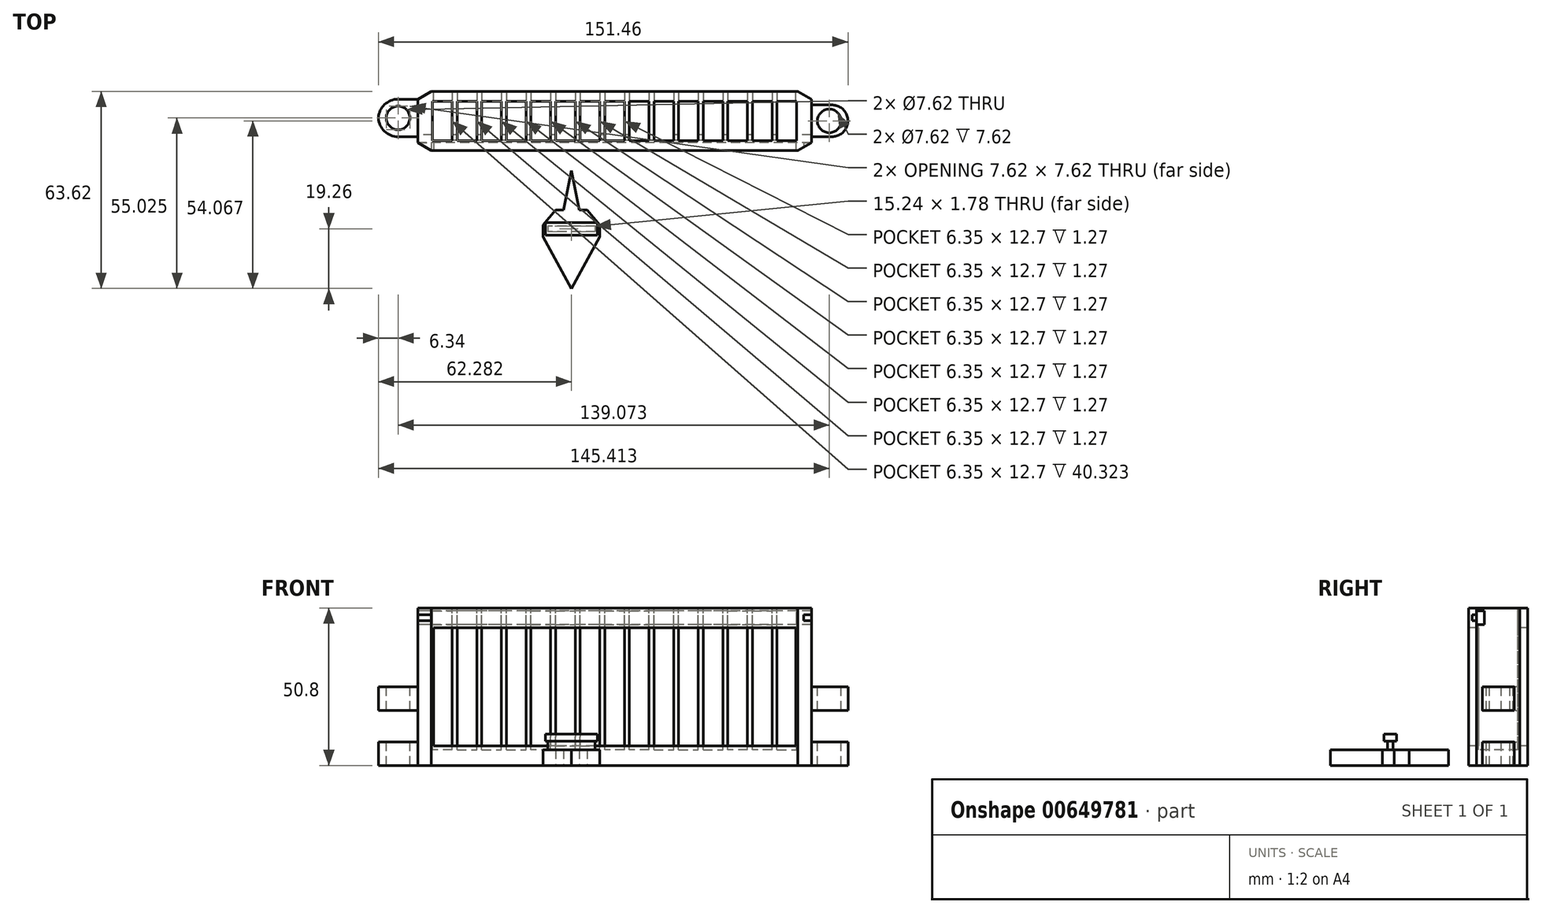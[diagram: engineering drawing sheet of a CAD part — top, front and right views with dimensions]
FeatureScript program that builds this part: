
annotation { "Feature Type Name" : "Feature", "Feature Type Description" : "" }
export const myFeature = defineFeature(function(context is Context, id is Id, definition is map)
    precondition{}
    {
        {
            var Q0;
            Q0=qCreatedBy(makeId("Front.planeOp"),FACE);
            var sketch = newSketch(context, id + "F0", { "sketchPlane" : qUnion([Q0])});
            skLineSegment(sketch, "E0", {"start": v(0, 0) * mm, "end": v(0, 50.8) * mm});
            skLineSegment(sketch, "E1.bottom", {"start": v(0, 50.8) * mm, "end": v(-63.5, 50.8) * mm});
            skLineSegment(sketch, "E1.top", {"start": v(0, 0) * mm, "end": v(-63.5, 0) * mm});
            skLineSegment(sketch, "E1.left", {"start": v(0, 50.8) * mm, "end": v(0, 0) * mm});
            skLineSegment(sketch, "E1.right", {"start": v(-63.5, 50.8) * mm, "end": v(-63.5, 0) * mm});
            skLineSegment(sketch, "E2.bottom", {"start": v(0, 50.8) * mm, "end": v(63.5, 50.8) * mm});
            skLineSegment(sketch, "E2.top", {"start": v(0, 0) * mm, "end": v(63.5, 0) * mm});
            skLineSegment(sketch, "E2.right", {"start": v(63.5, 50.8) * mm, "end": v(63.5, 0) * mm});
            skSolve(sketch);
        }
        {
            var Q0;
            Q0 = qSketchRegion(id + "F0", true);
            extrude(context, id + "F1", {"entities" : qUnion([Q0]), "depth" : 19.05 * mm, "offsetDistance" : 25.4 * mm});
        }
        {
            var Q0;
            Q0=makeQuery(id+"F1.opExtrude","SWEPT_FACE",FACE,{"disambiguationData":[OSD([sQuery(id+"F0.wireOp",EDGE,"E1.bottom"),sQuery(id+"F0.wireOp",EDGE,"E2.bottom")])]});
            var sketch = newSketch(context, id + "F2", { "sketchPlane" : qUnion([Q0])});
            skLineSegment(sketch, "E3.bottom", {"start": v(-63.5, 0) * mm, "end": v(63.5, 0) * mm});
            skLineSegment(sketch, "E3.top", {"start": v(-63.5, -19.05) * mm, "end": v(63.5, -19.05) * mm});
            skLineSegment(sketch, "E3.left", {"start": v(-63.5, 0) * mm, "end": v(-63.5, -19.05) * mm});
            skLineSegment(sketch, "E3.right", {"start": v(63.5, 0) * mm, "end": v(63.5, -19.05) * mm});
            skLineSegment(sketch, "E4", {"start": v(0, 0) * mm, "end": v(63.5, 0) * mm});
            skLineSegment(sketch, "E5", {"start": v(-63.5, 0) * mm, "end": v(0, 0) * mm});
            skLineSegment(sketch, "E6", {"start": v(31.75, -19.05) * mm, "end": v(63.5, -19.05) * mm});
            skLineSegment(sketch, "E7", {"start": v(0, -19.05) * mm, "end": v(31.75, -19.05) * mm});
            skLineSegment(sketch, "E8", {"start": v(-31.75, -19.05) * mm, "end": v(0, -19.05) * mm});
            skLineSegment(sketch, "E9", {"start": v(-63.5, -19.05) * mm, "end": v(-31.75, -19.05) * mm});
            skLineSegment(sketch, "E10", {"start": v(-47.63, 0) * mm, "end": v(-14.23, 0) * mm});
            skLineSegment(sketch, "E11", {"start": v(-15.88, 0) * mm, "end": v(-14.23, 0) * mm});
            skLineSegment(sketch, "E12", {"start": v(15.88, 0) * mm, "end": v(37.75, 0) * mm});
            skLineSegment(sketch, "E13", {"start": v(37.75, 0) * mm, "end": v(29.3, 0) * mm});
            skLineSegment(sketch, "E14", {"start": v(-63.5, 0) * mm, "end": v(-47.63, 0) * mm});
            skLineSegment(sketch, "E15.bottom", {"start": v(-52.39, -3.18) * mm, "end": v(-58.74, -3.18) * mm});
            skLineSegment(sketch, "E15.top", {"start": v(-52.39, -15.88) * mm, "end": v(-58.74, -15.88) * mm});
            skLineSegment(sketch, "E15.left", {"start": v(-52.39, -3.18) * mm, "end": v(-52.39, -15.88) * mm});
            skLineSegment(sketch, "E15.right", {"start": v(-58.74, -3.18) * mm, "end": v(-58.74, -15.88) * mm});
            skPoint(sketch, "E15.middle", {"position": v(-55.56, -9.53) * mm});
            skLineSegment(sketch, "E16.MirrorCS", {"start": v(-42.86, -3.18) * mm, "end": v(-42.86, -15.88) * mm});
            skLineSegment(sketch, "E17.MirrorCS", {"start": v(-42.86, -3.18) * mm, "end": v(-36.51, -3.18) * mm});
            skLineSegment(sketch, "E18.MirrorCS", {"start": v(-36.51, -3.18) * mm, "end": v(-36.51, -15.88) * mm});
            skLineSegment(sketch, "E19.MirrorCS", {"start": v(-42.86, -15.88) * mm, "end": v(-36.51, -15.88) * mm});
            skLineSegment(sketch, "E20.MirrorCS", {"start": v(-26.99, -3.18) * mm, "end": v(-26.99, -15.88) * mm});
            skLineSegment(sketch, "E21.MirrorCS", {"start": v(-20.64, -3.18) * mm, "end": v(-26.99, -3.18) * mm});
            skLineSegment(sketch, "E22.MirrorCS", {"start": v(-20.64, -3.18) * mm, "end": v(-20.64, -15.88) * mm});
            skLineSegment(sketch, "E23.MirrorCS", {"start": v(-20.64, -15.88) * mm, "end": v(-26.99, -15.88) * mm});
            skLineSegment(sketch, "E24.MirrorCS", {"start": v(-11.11, -15.88) * mm, "end": v(-4.76, -15.88) * mm});
            skLineSegment(sketch, "E25.MirrorCS", {"start": v(-4.76, -3.18) * mm, "end": v(-4.76, -15.88) * mm});
            skLineSegment(sketch, "E26.MirrorCS", {"start": v(-11.11, -3.18) * mm, "end": v(-4.76, -3.18) * mm});
            skLineSegment(sketch, "E27.MirrorCS", {"start": v(-11.11, -3.18) * mm, "end": v(-11.11, -15.88) * mm});
            skLineSegment(sketch, "E28.MirrorCS", {"start": v(11.11, -15.88) * mm, "end": v(4.76, -15.88) * mm});
            skLineSegment(sketch, "E29.MirrorCS", {"start": v(11.11, -3.18) * mm, "end": v(11.11, -15.88) * mm});
            skLineSegment(sketch, "E30.MirrorCS", {"start": v(4.76, -3.18) * mm, "end": v(4.76, -15.88) * mm});
            skLineSegment(sketch, "E31.MirrorCS", {"start": v(11.11, -3.18) * mm, "end": v(4.76, -3.18) * mm});
            skLineSegment(sketch, "E32.MirrorCS", {"start": v(26.99, -3.18) * mm, "end": v(26.99, -15.88) * mm});
            skLineSegment(sketch, "E33.MirrorCS", {"start": v(20.64, -15.88) * mm, "end": v(26.99, -15.88) * mm});
            skLineSegment(sketch, "E34.MirrorCS", {"start": v(20.64, -3.18) * mm, "end": v(20.64, -15.88) * mm});
            skLineSegment(sketch, "E35.MirrorCS", {"start": v(20.64, -3.18) * mm, "end": v(26.99, -3.18) * mm});
            skLineSegment(sketch, "E36.MirrorCS", {"start": v(42.86, -3.18) * mm, "end": v(36.51, -3.18) * mm});
            skLineSegment(sketch, "E37.MirrorCS", {"start": v(42.86, -3.18) * mm, "end": v(42.86, -15.88) * mm});
            skLineSegment(sketch, "E38.MirrorCS", {"start": v(36.51, -3.18) * mm, "end": v(36.51, -15.88) * mm});
            skLineSegment(sketch, "E39.MirrorCS", {"start": v(42.86, -15.88) * mm, "end": v(36.51, -15.88) * mm});
            skLineSegment(sketch, "E40.MirrorCS", {"start": v(52.39, -3.18) * mm, "end": v(52.39, -15.88) * mm});
            skLineSegment(sketch, "E41.MirrorCS", {"start": v(58.74, -3.18) * mm, "end": v(58.74, -15.88) * mm});
            skLineSegment(sketch, "E42.MirrorCS", {"start": v(52.39, -3.18) * mm, "end": v(58.74, -3.18) * mm});
            skLineSegment(sketch, "E43.MirrorCS", {"start": v(52.39, -15.88) * mm, "end": v(58.74, -15.88) * mm});
            skPoint(sketch, "E44.middle", {"position": v(-47.63, -9.53) * mm});
            skLineSegment(sketch, "E45.bottom", {"start": v(50.8, -3.18) * mm, "end": v(44.45, -3.18) * mm});
            skLineSegment(sketch, "E45.top", {"start": v(50.8, -15.88) * mm, "end": v(44.45, -15.88) * mm});
            skLineSegment(sketch, "E45.left", {"start": v(50.8, -3.18) * mm, "end": v(50.8, -15.88) * mm});
            skLineSegment(sketch, "E45.right", {"start": v(44.45, -3.18) * mm, "end": v(44.45, -15.88) * mm});
            skPoint(sketch, "E45.middle", {"position": v(47.62, -9.53) * mm});
            skLineSegment(sketch, "E46.MirrorCS", {"start": v(19.05, -3.18) * mm, "end": v(19.05, -15.88) * mm});
            skLineSegment(sketch, "E47.MirrorCS", {"start": v(12.7, -3.18) * mm, "end": v(19.05, -3.18) * mm});
            skLineSegment(sketch, "E48.MirrorCS", {"start": v(12.7, -3.18) * mm, "end": v(12.7, -15.88) * mm});
            skLineSegment(sketch, "E49.MirrorCS", {"start": v(12.7, -15.88) * mm, "end": v(19.05, -15.88) * mm});
            skLineSegment(sketch, "E50.MirrorCS", {"start": v(-12.7, -3.18) * mm, "end": v(-12.7, -15.88) * mm});
            skLineSegment(sketch, "E51.MirrorCS", {"start": v(-12.7, -3.18) * mm, "end": v(-19.05, -3.18) * mm});
            skLineSegment(sketch, "E52.MirrorCS", {"start": v(-19.05, -3.18) * mm, "end": v(-19.05, -15.88) * mm});
            skLineSegment(sketch, "E53.MirrorCS", {"start": v(-12.7, -15.88) * mm, "end": v(-19.05, -15.88) * mm});
            skLineSegment(sketch, "E54.MirrorCS", {"start": v(-44.45, -3.18) * mm, "end": v(-44.45, -15.88) * mm});
            skLineSegment(sketch, "E55.MirrorCS", {"start": v(-50.8, -15.88) * mm, "end": v(-44.45, -15.88) * mm});
            skLineSegment(sketch, "E56.MirrorCS", {"start": v(-50.8, -3.18) * mm, "end": v(-50.8, -15.88) * mm});
            skLineSegment(sketch, "E57.MirrorCS", {"start": v(-50.8, -3.18) * mm, "end": v(-44.45, -3.18) * mm});
            skLineSegment(sketch, "E58.bottom", {"start": v(3.18, -3.17) * mm, "end": v(-3.18, -3.17) * mm});
            skLineSegment(sketch, "E58.top", {"start": v(3.17, -15.88) * mm, "end": v(-3.18, -15.88) * mm});
            skLineSegment(sketch, "E58.left", {"start": v(3.18, -3.17) * mm, "end": v(3.17, -15.88) * mm});
            skLineSegment(sketch, "E58.right", {"start": v(-3.18, -3.17) * mm, "end": v(-3.18, -15.88) * mm});
            skPoint(sketch, "E58.middle", {"position": v(0, -9.53) * mm});
            skLineSegment(sketch, "E59.MirrorCS", {"start": v(28.57, -3.18) * mm, "end": v(28.57, -15.88) * mm});
            skLineSegment(sketch, "E60.MirrorCS", {"start": v(28.57, -15.88) * mm, "end": v(34.92, -15.88) * mm});
            skLineSegment(sketch, "E61.MirrorCS", {"start": v(34.92, -3.18) * mm, "end": v(34.92, -15.88) * mm});
            skLineSegment(sketch, "E62.MirrorCS", {"start": v(28.57, -3.18) * mm, "end": v(34.92, -3.18) * mm});
            skLineSegment(sketch, "E63.MirrorCS", {"start": v(-28.58, -3.17) * mm, "end": v(-28.58, -15.88) * mm});
            skLineSegment(sketch, "E64.MirrorCS", {"start": v(-34.93, -3.17) * mm, "end": v(-28.58, -3.17) * mm});
            skLineSegment(sketch, "E65.MirrorCS", {"start": v(-34.93, -3.17) * mm, "end": v(-34.93, -15.88) * mm});
            skLineSegment(sketch, "E66.MirrorCS", {"start": v(-34.93, -15.88) * mm, "end": v(-28.58, -15.88) * mm});
            skSolve(sketch);
        }
        {
            var Q0;
            Q0=makeQuery(id+"F2.imprint","IMPRINT",FACE,{"disambiguationData":[TD([[makeQuery(id+"F2.imprint","IMPRINT",EDGE,{"derivedFrom":sQuery(id+"F2.wireOp",EDGE,"E15.bottom")}),1.0]])]});
            var Q1;
            Q1=makeQuery(id+"F2.imprint","IMPRINT",FACE,{"disambiguationData":[TD([[makeQuery(id+"F2.imprint","IMPRINT",EDGE,{"derivedFrom":sQuery(id+"F2.wireOp",EDGE,"E54.MirrorCS")}),-1.0]])]});
            var Q2;
            Q2=makeQuery(id+"F2.imprint","IMPRINT",FACE,{"disambiguationData":[TD([[makeQuery(id+"F2.imprint","IMPRINT",EDGE,{"derivedFrom":sQuery(id+"F2.wireOp",EDGE,"E16.MirrorCS")}),1.0]])]});
            var Q3;
            Q3=makeQuery(id+"F2.imprint","IMPRINT",FACE,{"disambiguationData":[TD([[makeQuery(id+"F2.imprint","IMPRINT",EDGE,{"derivedFrom":sQuery(id+"F2.wireOp",EDGE,"E63.MirrorCS")}),-1.0]])]});
            var Q4;
            Q4=makeQuery(id+"F2.imprint","IMPRINT",FACE,{"disambiguationData":[TD([[makeQuery(id+"F2.imprint","IMPRINT",EDGE,{"derivedFrom":sQuery(id+"F2.wireOp",EDGE,"E20.MirrorCS")}),1.0]])]});
            var Q5;
            Q5=makeQuery(id+"F2.imprint","IMPRINT",FACE,{"disambiguationData":[TD([[makeQuery(id+"F2.imprint","IMPRINT",EDGE,{"derivedFrom":sQuery(id+"F2.wireOp",EDGE,"E50.MirrorCS")}),-1.0]])]});
            var Q6;
            Q6=makeQuery(id+"F2.imprint","IMPRINT",FACE,{"disambiguationData":[TD([[makeQuery(id+"F2.imprint","IMPRINT",EDGE,{"derivedFrom":sQuery(id+"F2.wireOp",EDGE,"E24.MirrorCS")}),1.0]])]});
            var Q7;
            Q7=makeQuery(id+"F2.imprint","IMPRINT",FACE,{"disambiguationData":[TD([[makeQuery(id+"F2.imprint","IMPRINT",EDGE,{"derivedFrom":sQuery(id+"F2.wireOp",EDGE,"E58.bottom")}),1.0]])]});
            var Q8;
            Q8=makeQuery(id+"F2.imprint","IMPRINT",FACE,{"disambiguationData":[TD([[makeQuery(id+"F2.imprint","IMPRINT",EDGE,{"derivedFrom":sQuery(id+"F2.wireOp",EDGE,"E28.MirrorCS")}),-1.0]])]});
            var Q9;
            Q9=makeQuery(id+"F2.imprint","IMPRINT",FACE,{"disambiguationData":[TD([[makeQuery(id+"F2.imprint","IMPRINT",EDGE,{"derivedFrom":sQuery(id+"F2.wireOp",EDGE,"E46.MirrorCS")}),-1.0]])]});
            var Q10;
            Q10=makeQuery(id+"F2.imprint","IMPRINT",FACE,{"disambiguationData":[TD([[makeQuery(id+"F2.imprint","IMPRINT",EDGE,{"derivedFrom":sQuery(id+"F2.wireOp",EDGE,"E32.MirrorCS")}),-1.0]])]});
            var Q11;
            Q11=makeQuery(id+"F2.imprint","IMPRINT",FACE,{"disambiguationData":[TD([[makeQuery(id+"F2.imprint","IMPRINT",EDGE,{"derivedFrom":sQuery(id+"F2.wireOp",EDGE,"E59.MirrorCS")}),1.0]])]});
            var Q12;
            Q12=makeQuery(id+"F2.imprint","IMPRINT",FACE,{"disambiguationData":[TD([[makeQuery(id+"F2.imprint","IMPRINT",EDGE,{"derivedFrom":sQuery(id+"F2.wireOp",EDGE,"E36.MirrorCS")}),1.0]])]});
            var Q13;
            Q13=makeQuery(id+"F2.imprint","IMPRINT",FACE,{"disambiguationData":[TD([[makeQuery(id+"F2.imprint","IMPRINT",EDGE,{"derivedFrom":sQuery(id+"F2.wireOp",EDGE,"E45.bottom")}),1.0]])]});
            var Q14;
            Q14=makeQuery(id+"F2.imprint","IMPRINT",FACE,{"disambiguationData":[TD([[makeQuery(id+"F2.imprint","IMPRINT",EDGE,{"derivedFrom":sQuery(id+"F2.wireOp",EDGE,"E40.MirrorCS")}),1.0]])]});
            extrude(context, id + "F3", {"entities" : qUnion([Q0, Q1, Q2, Q3, Q4, Q5, Q6, Q7, Q8, Q9, Q10, Q11, Q12, Q13, Q14]), "operationType" : NewBodyOperationType.REMOVE, "oppositeDirection" : true, "depth" : 45.72 * mm, "offsetDistance" : 25.4 * mm});
        }
        {
            var Q0;
            Q0=makeQuery(id+"F1.opExtrude","CAP_FACE",FACE,{"disambiguationData":[OSD([sQuery(id+"F0.wireOp",EDGE,"E1.bottom"),sQuery(id+"F0.wireOp",EDGE,"E1.top"),sQuery(id+"F0.wireOp",EDGE,"E1.right"),sQuery(id+"F0.wireOp",EDGE,"E2.bottom"),sQuery(id+"F0.wireOp",EDGE,"E2.top"),sQuery(id+"F0.wireOp",EDGE,"E2.right")])],"isStart":false});
            var sketch = newSketch(context, id + "F4", { "sketchPlane" : qUnion([Q0])});
            skLineSegment(sketch, "E67.bottom", {"start": v(-63.5, 50.8) * mm, "end": v(63.5, 50.8) * mm});
            skLineSegment(sketch, "E67.top", {"start": v(-63.5, 0) * mm, "end": v(63.5, 0) * mm});
            skLineSegment(sketch, "E67.left", {"start": v(-63.5, 50.8) * mm, "end": v(-63.5, 0) * mm});
            skLineSegment(sketch, "E67.right", {"start": v(63.5, 50.8) * mm, "end": v(63.5, 0) * mm});
            skLineSegment(sketch, "E68", {"start": v(0, 50.8) * mm, "end": v(0, 0) * mm});
            skLineSegment(sketch, "E69.bottom", {"start": v(58.42, 44.45) * mm, "end": v(-58.42, 44.45) * mm});
            skLineSegment(sketch, "E69.top", {"start": v(58.42, 6.35) * mm, "end": v(-58.42, 6.35) * mm});
            skLineSegment(sketch, "E69.left", {"start": v(58.42, 44.45) * mm, "end": v(58.42, 6.35) * mm});
            skLineSegment(sketch, "E69.right", {"start": v(-58.42, 44.45) * mm, "end": v(-58.42, 6.35) * mm});
            skPoint(sketch, "E69.middle", {"position": v(0, 25.4) * mm});
            skSolve(sketch);
        }
        {
            var Q0;
            {var subQ5=sQuery(id+"F4.wireOp",EDGE,"E69.right");Q0=makeQuery(id+"F4.imprint","IMPRINT",FACE,{"disambiguationData":[TD([[makeQuery(id+"F4.imprint","IMPRINT",EDGE,{"derivedFrom":subQ5}),1.0]])]});}
            var Q1;
            {var subQ5=sQuery(id+"F4.wireOp",EDGE,"E69.left");Q1=makeQuery(id+"F4.imprint","IMPRINT",FACE,{"disambiguationData":[TD([[makeQuery(id+"F4.imprint","IMPRINT",EDGE,{"derivedFrom":subQ5}),-1.0]])]});}
            extrude(context, id + "F5", {"entities" : qUnion([Q0, Q1]), "operationType" : NewBodyOperationType.REMOVE, "oppositeDirection" : true, "depth" : 3.3 * mm, "offsetDistance" : 25.4 * mm});
        }
        {
            var Q0;
            Q0=makeQuery(id+"F1.opExtrude","CAP_FACE",FACE,{"disambiguationData":[OSD([sQuery(id+"F0.wireOp",EDGE,"E1.bottom"),sQuery(id+"F0.wireOp",EDGE,"E1.top"),sQuery(id+"F0.wireOp",EDGE,"E1.right"),sQuery(id+"F0.wireOp",EDGE,"E2.bottom"),sQuery(id+"F0.wireOp",EDGE,"E2.top"),sQuery(id+"F0.wireOp",EDGE,"E2.right")])],"isStart":true});
            var sketch = newSketch(context, id + "F6", { "sketchPlane" : qUnion([Q0])});
            skLineSegment(sketch, "E70.bottom", {"start": v(-63.5, 50.8) * mm, "end": v(63.5, 50.8) * mm});
            skLineSegment(sketch, "E70.top", {"start": v(-63.5, 0) * mm, "end": v(63.5, 0) * mm});
            skLineSegment(sketch, "E70.left", {"start": v(-63.5, 50.8) * mm, "end": v(-63.5, 0) * mm});
            skLineSegment(sketch, "E70.right", {"start": v(63.5, 50.8) * mm, "end": v(63.5, 0) * mm});
            skLineSegment(sketch, "E71", {"start": v(0, 50.8) * mm, "end": v(0, 0) * mm});
            skLineSegment(sketch, "E72.bottom", {"start": v(58.42, 44.45) * mm, "end": v(-58.42, 44.45) * mm});
            skLineSegment(sketch, "E72.top", {"start": v(58.42, 6.35) * mm, "end": v(-58.42, 6.35) * mm});
            skLineSegment(sketch, "E72.left", {"start": v(58.42, 44.45) * mm, "end": v(58.42, 6.35) * mm});
            skLineSegment(sketch, "E72.right", {"start": v(-58.42, 44.45) * mm, "end": v(-58.42, 6.35) * mm});
            skPoint(sketch, "E72.middle", {"position": v(0, 25.4) * mm});
            skSolve(sketch);
        }
        {
            var Q0;
            {var subQ5=sQuery(id+"F6.wireOp",EDGE,"E72.left");Q0=makeQuery(id+"F6.imprint","IMPRINT",FACE,{"disambiguationData":[TD([[makeQuery(id+"F6.imprint","IMPRINT",EDGE,{"derivedFrom":subQ5}),-1.0]])]});}
            var Q1;
            {var subQ5=sQuery(id+"F6.wireOp",EDGE,"E72.right");Q1=makeQuery(id+"F6.imprint","IMPRINT",FACE,{"disambiguationData":[TD([[makeQuery(id+"F6.imprint","IMPRINT",EDGE,{"derivedFrom":subQ5}),1.0]])]});}
            extrude(context, id + "F7", {"entities" : qUnion([Q0, Q1]), "operationType" : NewBodyOperationType.REMOVE, "oppositeDirection" : true, "depth" : 3.3 * mm, "offsetDistance" : 25.4 * mm});
        }
        {
            var Q0;
            Q0=makeQuery(id+"F5.boolean.opBoolean","COPY",EDGE,{"derivedFrom":makeQuery(id+"F5.opExtrude","CAP_EDGE",EDGE,{"disambiguationData":[OSD([sQuery(id+"F4.wireOp",EDGE,"E69.top")])],"isStart":true})});
            var Q1;
            Q1=makeQuery(id+"F1.opExtrude","CAP_EDGE",EDGE,{"disambiguationData":[OSD([sQuery(id+"F0.wireOp",EDGE,"E2.right")])],"isStart":false});
            var Q2;
            Q2=makeQuery(id+"F1.opExtrude","CAP_EDGE",EDGE,{"disambiguationData":[OSD([sQuery(id+"F0.wireOp",EDGE,"E2.right")])],"isStart":true});
            var Q3;
            Q3=makeQuery(id+"F1.opExtrude","CAP_EDGE",EDGE,{"disambiguationData":[OSD([sQuery(id+"F0.wireOp",EDGE,"E1.right")])],"isStart":false});
            var Q4;
            Q4=makeQuery(id+"F1.opExtrude","CAP_EDGE",EDGE,{"disambiguationData":[OSD([sQuery(id+"F0.wireOp",EDGE,"E1.right")])],"isStart":true});
            chamfer(context, id + "F8", {"entities" : qUnion([Q0, Q1, Q2, Q3, Q4]), "chamferType" : ChamferType.OFFSET_ANGLE, "width" : 2.54 * mm, "oppositeDirection" : false, "angle" : 60 * degree, "tangentPropagation" : true});
        }
        {
            var Q0;
            Q0=makeQuery(id+"F1.opExtrude","CAP_FACE",FACE,{"disambiguationData":[OSD([sQuery(id+"F0.wireOp",EDGE,"E1.bottom"),sQuery(id+"F0.wireOp",EDGE,"E1.top"),sQuery(id+"F0.wireOp",EDGE,"E1.right"),sQuery(id+"F0.wireOp",EDGE,"E2.bottom"),sQuery(id+"F0.wireOp",EDGE,"E2.top"),sQuery(id+"F0.wireOp",EDGE,"E2.right")])],"isStart":false});
            var sketch = newSketch(context, id + "F9", { "sketchPlane" : qUnion([Q0])});
            skLineSegment(sketch, "E73.bottom", {"start": v(60.96, 50.8) * mm, "end": v(-60.96, 50.8) * mm});
            skLineSegment(sketch, "E73.top", {"start": v(60.96, 44.45) * mm, "end": v(-60.96, 44.45) * mm});
            skLineSegment(sketch, "E73.left", {"start": v(60.96, 50.8) * mm, "end": v(60.96, 44.45) * mm});
            skLineSegment(sketch, "E73.right", {"start": v(-60.96, 50.8) * mm, "end": v(-60.96, 44.45) * mm});
            skLineSegment(sketch, "E74", {"start": v(0, 44.45) * mm, "end": v(0, 50.8) * mm});
            skLineSegment(sketch, "E75.bottom", {"start": v(-76.2, 48.58) * mm, "end": v(76.2, 48.58) * mm});
            skLineSegment(sketch, "E75.top", {"start": v(-76.2, 46.67) * mm, "end": v(76.2, 46.67) * mm});
            skLineSegment(sketch, "E75.left", {"start": v(-76.2, 48.58) * mm, "end": v(-76.2, 46.67) * mm});
            skLineSegment(sketch, "E75.right", {"start": v(76.2, 48.58) * mm, "end": v(76.2, 46.67) * mm});
            skPoint(sketch, "E75.middle", {"position": v(0, 47.62) * mm});
            skSolve(sketch);
        }
        {
            var Q0;
            {var subQ5=sQuery(id+"F9.wireOp",EDGE,"E75.right");Q0=makeQuery(id+"F9.imprint","IMPRINT",FACE,{"disambiguationData":[TD([[makeQuery(id+"F9.imprint","IMPRINT",EDGE,{"derivedFrom":subQ5}),-1.0]])]});}
            var Q1;
            {var subQ5=sQuery(id+"F9.wireOp",EDGE,"E75.left");Q1=makeQuery(id+"F9.imprint","IMPRINT",FACE,{"disambiguationData":[TD([[makeQuery(id+"F9.imprint","IMPRINT",EDGE,{"derivedFrom":subQ5}),1.0]])]});}
            var Q2;
            {var subQ0=sQuery(id+"F9.wireOp",EDGE,"E75.top");var subQ1=sQuery(id+"F9.wireOp",EDGE,"E73.left");var subQ2=makeQuery(id+"F9.imprint","INTERSECT",VERTEX,{"derivedFrom":[subQ1,subQ0]});Q2=makeQuery(id+"F9.imprint","IMPRINT",FACE,{"disambiguationData":[TD([[makeQuery(id+"F9.imprint","IMPRINT",EDGE,{"disambiguationData":[TD([[subQ2,-1.0]])],"derivedFrom":subQ1}),1.0]])]});}
            var Q3;
            {var subQ0=sQuery(id+"F9.wireOp",EDGE,"E75.bottom");var subQ1=sQuery(id+"F9.wireOp",EDGE,"E73.right");var subQ2=makeQuery(id+"F9.imprint","INTERSECT",VERTEX,{"derivedFrom":[subQ1,subQ0]});Q3=makeQuery(id+"F9.imprint","IMPRINT",FACE,{"disambiguationData":[TD([[makeQuery(id+"F9.imprint","IMPRINT",EDGE,{"disambiguationData":[TD([[subQ2,-1.0]])],"derivedFrom":subQ1}),1.0]])]});}
            extrude(context, id + "F10", {"entities" : qUnion([Q0, Q1, Q2, Q3]), "operationType" : NewBodyOperationType.REMOVE, "oppositeDirection" : true, "depth" : 2.54 * mm, "offsetDistance" : 25.4 * mm});
        }
        {
            var Q0;
            Q0=makeQuery(id+"F10.boolean.opBoolean","COPY",FACE,{"derivedFrom":makeQuery(id+"F10.opExtrude","CAP_FACE",FACE,{"disambiguationData":[OSD([sQuery(id+"F9.wireOp",EDGE,"E75.bottom"),sQuery(id+"F9.wireOp",EDGE,"E75.top"),sQuery(id+"F9.wireOp",EDGE,"E75.left"),sQuery(id+"F9.wireOp",EDGE,"E75.right")])],"isStart":false})});
            var sketch = newSketch(context, id + "F11", { "sketchPlane" : qUnion([Q0])});
            skLineSegment(sketch, "E76.bottom", {"start": v(60.96, 48.58) * mm, "end": v(-62.43, 48.58) * mm});
            skLineSegment(sketch, "E76.top", {"start": v(60.96, 46.67) * mm, "end": v(-62.43, 46.67) * mm});
            skLineSegment(sketch, "E76.left", {"start": v(60.96, 48.58) * mm, "end": v(60.96, 46.67) * mm});
            skLineSegment(sketch, "E76.right", {"start": v(-62.43, 48.58) * mm, "end": v(-62.43, 46.67) * mm});
            skLineSegment(sketch, "E77", {"start": v(0, 48.58) * mm, "end": v(0, 46.67) * mm});
            skPoint(sketch, "E77.endSnap0", {"position": v(0, 46.67) * mm});
            skLineSegment(sketch, "E78.bottom", {"start": v(77.64, 49.85) * mm, "end": v(-77.64, 49.85) * mm});
            skLineSegment(sketch, "E78.top", {"start": v(77.64, 45.4) * mm, "end": v(-77.64, 45.4) * mm});
            skLineSegment(sketch, "E78.left", {"start": v(77.64, 49.85) * mm, "end": v(77.64, 45.4) * mm});
            skLineSegment(sketch, "E78.right", {"start": v(-77.64, 49.85) * mm, "end": v(-77.64, 45.4) * mm});
            skPoint(sketch, "E78.middle", {"position": v(0, 47.62) * mm});
            skSolve(sketch);
        }
        {
            var Q0;
            {var subQ0=sQuery(id+"F11.wireOp",EDGE,"E76.right");Q0=makeQuery(id+"F11.imprint","IMPRINT",FACE,{"disambiguationData":[TD([[makeQuery(id+"F11.imprint","IMPRINT",EDGE,{"derivedFrom":subQ0}),1.0]])]});}
            var Q1;
            {var subQ0=sQuery(id+"F11.wireOp",EDGE,"E76.left");Q1=makeQuery(id+"F11.imprint","IMPRINT",FACE,{"disambiguationData":[TD([[makeQuery(id+"F11.imprint","IMPRINT",EDGE,{"derivedFrom":subQ0}),-1.0]])]});}
            var Q2;
            {var subQ0=sQuery(id+"F11.wireOp",EDGE,"E76.left");Q2=makeQuery(id+"F11.imprint","IMPRINT",FACE,{"disambiguationData":[TD([[makeQuery(id+"F11.imprint","IMPRINT",EDGE,{"derivedFrom":subQ0}),1.0]])]});}
            var Q3;
            {var subQ0=sQuery(id+"F11.wireOp",EDGE,"E76.right");Q3=makeQuery(id+"F11.imprint","IMPRINT",FACE,{"disambiguationData":[TD([[makeQuery(id+"F11.imprint","IMPRINT",EDGE,{"derivedFrom":subQ0}),-1.0]])]});}
            extrude(context, id + "F12", {"entities" : qUnion([Q0, Q1, Q2, Q3]), "operationType" : NewBodyOperationType.REMOVE, "oppositeDirection" : true, "depth" : 2.54 * mm, "offsetDistance" : 25.4 * mm});
        }
        {
            var Q0;
            Q0=qCreatedBy(makeId("Top.planeOp"),FACE);
            var sketch = newSketch(context, id + "F13", { "sketchPlane" : qUnion([Q0])});
            skLineSegment(sketch, "E79", {"start": v(-8.83, -38.22) * mm, "end": v(-4.75, -43.09) * mm});
            skLineSegment(sketch, "E80", {"start": v(-18.99, -38.22) * mm, "end": v(-23.07, -43.09) * mm});
            skLineSegment(sketch, "E81", {"start": v(-23.07, -43.09) * mm, "end": v(-23.07, -46.9) * mm});
            skLineSegment(sketch, "E82", {"start": v(-4.75, -43.09) * mm, "end": v(-4.75, -46.9) * mm});
            skLineSegment(sketch, "E83", {"start": v(-23.07, -46.9) * mm, "end": v(-13.9, -63.62) * mm});
            skLineSegment(sketch, "E84", {"start": v(-4.75, -46.9) * mm, "end": v(-13.9, -63.62) * mm});
            skLineSegment(sketch, "E85", {"start": v(-13.9, -38.22) * mm, "end": v(-13.9, -25.52) * mm});
            skLineSegment(sketch, "E86", {"start": v(-18.99, -38.22) * mm, "end": v(-13.9, -38.22) * mm});
            skLineSegment(sketch, "E87", {"start": v(-8.83, -38.22) * mm, "end": v(-13.9, -38.22) * mm});
            skLineSegment(sketch, "E88", {"start": v(-16.45, -38.22) * mm, "end": v(-13.9, -25.52) * mm});
            skLineSegment(sketch, "E89", {"start": v(-11.37, -38.22) * mm, "end": v(-13.9, -25.52) * mm});
            skSolve(sketch);
        }
        {
            var Q0;
            Q0 = qSketchRegion(id + "F13", true);
            extrude(context, id + "F14", {"entities" : qUnion([Q0]), "depth" : 5.08 * mm, "offsetDistance" : 25.4 * mm});
        }
        {
            var Q0;
            Q0=makeQuery(id+"F14.opExtrude","CAP_FACE",FACE,{"disambiguationData":[OSD([sQuery(id+"F13.wireOp",EDGE,"0yB4nnRf-JXvP-dkhB-26Qb-3KcpkU1DMZCn"),sQuery(id+"F13.wireOp",EDGE,"E79"),sQuery(id+"F13.wireOp",EDGE,"E80"),sQuery(id+"F13.wireOp",EDGE,"E81"),sQuery(id+"F13.wireOp",EDGE,"E82"),sQuery(id+"F13.wireOp",EDGE,"E83"),sQuery(id+"F13.wireOp",EDGE,"E84")])],"isStart":false});
            var sketch = newSketch(context, id + "F15", { "sketchPlane" : qUnion([Q0])});
            skLineSegment(sketch, "E90.bottom", {"start": v(-6.29, -43.47) * mm, "end": v(-21.53, -43.47) * mm});
            skLineSegment(sketch, "E90.top", {"start": v(-6.29, -45.25) * mm, "end": v(-21.53, -45.25) * mm});
            skLineSegment(sketch, "E90.left", {"start": v(-6.29, -43.47) * mm, "end": v(-6.29, -45.25) * mm});
            skLineSegment(sketch, "E90.right", {"start": v(-21.53, -43.47) * mm, "end": v(-21.53, -45.25) * mm});
            skPoint(sketch, "E90.middle", {"position": v(-13.9, -44.36) * mm});
            skSolve(sketch);
        }
        {
            var Q0;
            Q0 = qSketchRegion(id + "F15", true);
            extrude(context, id + "F16", {"entities" : qUnion([Q0]), "operationType" : NewBodyOperationType.ADD, "depth" : 2.8 * mm, "offsetDistance" : 25.4 * mm});
        }
        {
            var Q0;
            Q0=makeQuery(id+"F16.opExtrude","CAP_FACE",FACE,{"disambiguationData":[OSD([sQuery(id+"F15.wireOp",EDGE,"E90.bottom"),sQuery(id+"F15.wireOp",EDGE,"E90.top"),sQuery(id+"F15.wireOp",EDGE,"E90.left"),sQuery(id+"F15.wireOp",EDGE,"E90.right")])],"isStart":false});
            var sketch = newSketch(context, id + "F17", { "sketchPlane" : qUnion([Q0])});
            skLineSegment(sketch, "E91", {"start": v(-21.53, -43.47) * mm, "end": v(-6.29, -45.25) * mm});
            skLineSegment(sketch, "E92.bottom", {"start": v(-5.53, -42.33) * mm, "end": v(-22.29, -42.33) * mm});
            skLineSegment(sketch, "E92.top", {"start": v(-5.53, -46.4) * mm, "end": v(-22.29, -46.4) * mm});
            skLineSegment(sketch, "E92.left", {"start": v(-5.53, -42.33) * mm, "end": v(-5.53, -46.4) * mm});
            skLineSegment(sketch, "E92.right", {"start": v(-22.29, -42.33) * mm, "end": v(-22.29, -46.4) * mm});
            skPoint(sketch, "E92.middle", {"position": v(-13.9, -44.36) * mm});
            skSolve(sketch);
        }
        {
            var Q0;
            Q0=makeQuery(id+"F17.imprint","IMPRINT",FACE,{"disambiguationData":[TD([[makeQuery(id+"F17.imprint","IMPRINT",EDGE,{"derivedFrom":sQuery(id+"F17.wireOp",EDGE,"E92.bottom")}),1.0]])]});
            var Q1;
            Q1=makeQuery(id+"F17.imprint","IMPRINT",FACE,{"disambiguationData":[TD([[makeQuery(id+"F17.imprint","IMPRINT",EDGE,{"derivedFrom":sQuery(id+"F17.wireOp",EDGE,"E91")}),1.0]])]});
            var Q2;
            Q2=makeQuery(id+"F17.imprint","IMPRINT",FACE,{"disambiguationData":[TD([[makeQuery(id+"F17.imprint","IMPRINT",EDGE,{"derivedFrom":sQuery(id+"F17.wireOp",EDGE,"E91")}),-1.0]])]});
            extrude(context, id + "F18", {"entities" : qUnion([Q0, Q1, Q2]), "operationType" : NewBodyOperationType.ADD, "depth" : 2.3 * mm, "offsetDistance" : 25.4 * mm});
        }
        {
            var Q0;
            {var subQ0=sQuery(id+"F6.wireOp",EDGE,"E72.top");var subQ1=sQuery(id+"F6.wireOp",EDGE,"E72.bottom");Q0=makeQuery(id+"F7.boolean.opBoolean","COPY",FACE,{"disambiguationData":[TD([makeQuery(id+"F3.boolean.opBoolean","COPY",FACE,{"derivedFrom":makeQuery(id+"F3.opExtrude","SWEPT_FACE",FACE,{"disambiguationData":[OSD([sQuery(id+"F2.wireOp",EDGE,"E40.MirrorCS")])]})})])],"derivedFrom":makeQuery(id+"F7.opExtrude","CAP_FACE",FACE,{"disambiguationData":[OSD([subQ1,subQ0,sQuery(id+"F6.wireOp",EDGE,"E72.left"),sQuery(id+"F6.wireOp",EDGE,"E72.right")])],"isStart":false})});}
            var Q1;
            {var subQ0=sQuery(id+"F6.wireOp",EDGE,"E72.bottom");var subQ1=sQuery(id+"F6.wireOp",EDGE,"E72.top");Q1=makeQuery(id+"F7.boolean.opBoolean","COPY",FACE,{"disambiguationData":[TD([makeQuery(id+"F3.boolean.opBoolean","COPY",FACE,{"derivedFrom":makeQuery(id+"F3.opExtrude","SWEPT_FACE",FACE,{"disambiguationData":[OSD([sQuery(id+"F2.wireOp",EDGE,"E37.MirrorCS")])]})})])],"derivedFrom":makeQuery(id+"F7.opExtrude","CAP_FACE",FACE,{"disambiguationData":[OSD([subQ0,subQ1,sQuery(id+"F6.wireOp",EDGE,"E72.left"),sQuery(id+"F6.wireOp",EDGE,"E72.right")])],"isStart":false})});}
            var Q2;
            {var subQ0=sQuery(id+"F6.wireOp",EDGE,"E72.bottom");var subQ1=sQuery(id+"F6.wireOp",EDGE,"E72.top");Q2=makeQuery(id+"F7.boolean.opBoolean","COPY",FACE,{"disambiguationData":[TD([makeQuery(id+"F3.boolean.opBoolean","COPY",FACE,{"derivedFrom":makeQuery(id+"F3.opExtrude","SWEPT_FACE",FACE,{"disambiguationData":[OSD([sQuery(id+"F2.wireOp",EDGE,"E38.MirrorCS")])]})})])],"derivedFrom":makeQuery(id+"F7.opExtrude","CAP_FACE",FACE,{"disambiguationData":[OSD([subQ0,subQ1,sQuery(id+"F6.wireOp",EDGE,"E72.left"),sQuery(id+"F6.wireOp",EDGE,"E72.right")])],"isStart":false})});}
            var Q3;
            {var subQ0=sQuery(id+"F6.wireOp",EDGE,"E72.top");var subQ1=sQuery(id+"F6.wireOp",EDGE,"E72.bottom");Q3=makeQuery(id+"F7.boolean.opBoolean","COPY",FACE,{"disambiguationData":[TD([makeQuery(id+"F3.boolean.opBoolean","COPY",FACE,{"derivedFrom":makeQuery(id+"F3.opExtrude","SWEPT_FACE",FACE,{"disambiguationData":[OSD([sQuery(id+"F2.wireOp",EDGE,"E32.MirrorCS")])]})})])],"derivedFrom":makeQuery(id+"F7.opExtrude","CAP_FACE",FACE,{"disambiguationData":[OSD([subQ1,subQ0,sQuery(id+"F6.wireOp",EDGE,"E72.left"),sQuery(id+"F6.wireOp",EDGE,"E72.right")])],"isStart":false})});}
            var Q4;
            {var subQ0=sQuery(id+"F6.wireOp",EDGE,"E72.top");var subQ1=sQuery(id+"F6.wireOp",EDGE,"E72.bottom");Q4=makeQuery(id+"F7.boolean.opBoolean","COPY",FACE,{"disambiguationData":[TD([makeQuery(id+"F3.boolean.opBoolean","COPY",FACE,{"derivedFrom":makeQuery(id+"F3.opExtrude","SWEPT_FACE",FACE,{"disambiguationData":[OSD([sQuery(id+"F2.wireOp",EDGE,"E34.MirrorCS")])]})})])],"derivedFrom":makeQuery(id+"F7.opExtrude","CAP_FACE",FACE,{"disambiguationData":[OSD([subQ1,subQ0,sQuery(id+"F6.wireOp",EDGE,"E72.left"),sQuery(id+"F6.wireOp",EDGE,"E72.right")])],"isStart":false})});}
            var Q5;
            {var subQ0=sQuery(id+"F6.wireOp",EDGE,"E72.bottom");var subQ1=sQuery(id+"F6.wireOp",EDGE,"E72.top");Q5=makeQuery(id+"F7.boolean.opBoolean","COPY",FACE,{"disambiguationData":[TD([makeQuery(id+"F3.boolean.opBoolean","COPY",FACE,{"derivedFrom":makeQuery(id+"F3.opExtrude","SWEPT_FACE",FACE,{"disambiguationData":[OSD([sQuery(id+"F2.wireOp",EDGE,"E29.MirrorCS")])]})})])],"derivedFrom":makeQuery(id+"F7.opExtrude","CAP_FACE",FACE,{"disambiguationData":[OSD([subQ0,subQ1,sQuery(id+"F6.wireOp",EDGE,"E72.left"),sQuery(id+"F6.wireOp",EDGE,"E72.right")])],"isStart":false})});}
            var Q6;
            {var subQ0=sQuery(id+"F6.wireOp",EDGE,"E72.bottom");var subQ1=sQuery(id+"F6.wireOp",EDGE,"E72.top");Q6=makeQuery(id+"F7.boolean.opBoolean","COPY",FACE,{"disambiguationData":[TD([makeQuery(id+"F3.boolean.opBoolean","COPY",FACE,{"derivedFrom":makeQuery(id+"F3.opExtrude","SWEPT_FACE",FACE,{"disambiguationData":[OSD([sQuery(id+"F2.wireOp",EDGE,"E30.MirrorCS")])]})})])],"derivedFrom":makeQuery(id+"F7.opExtrude","CAP_FACE",FACE,{"disambiguationData":[OSD([subQ0,subQ1,sQuery(id+"F6.wireOp",EDGE,"E72.left"),sQuery(id+"F6.wireOp",EDGE,"E72.right")])],"isStart":false})});}
            var Q7;
            {var subQ0=sQuery(id+"F6.wireOp",EDGE,"E72.bottom");var subQ1=sQuery(id+"F6.wireOp",EDGE,"E72.top");Q7=makeQuery(id+"F7.boolean.opBoolean","COPY",FACE,{"disambiguationData":[TD([makeQuery(id+"F3.boolean.opBoolean","COPY",FACE,{"derivedFrom":makeQuery(id+"F3.opExtrude","SWEPT_FACE",FACE,{"disambiguationData":[OSD([sQuery(id+"F2.wireOp",EDGE,"E25.MirrorCS")])]})})])],"derivedFrom":makeQuery(id+"F7.opExtrude","CAP_FACE",FACE,{"disambiguationData":[OSD([subQ0,subQ1,sQuery(id+"F6.wireOp",EDGE,"E72.left"),sQuery(id+"F6.wireOp",EDGE,"E72.right")])],"isStart":false})});}
            var Q8;
            {var subQ0=sQuery(id+"F6.wireOp",EDGE,"E72.top");var subQ1=sQuery(id+"F6.wireOp",EDGE,"E72.bottom");Q8=makeQuery(id+"F7.boolean.opBoolean","COPY",FACE,{"disambiguationData":[TD([makeQuery(id+"F3.boolean.opBoolean","COPY",FACE,{"derivedFrom":makeQuery(id+"F3.opExtrude","SWEPT_FACE",FACE,{"disambiguationData":[OSD([sQuery(id+"F2.wireOp",EDGE,"E27.MirrorCS")])]})})])],"derivedFrom":makeQuery(id+"F7.opExtrude","CAP_FACE",FACE,{"disambiguationData":[OSD([subQ1,subQ0,sQuery(id+"F6.wireOp",EDGE,"E72.left"),sQuery(id+"F6.wireOp",EDGE,"E72.right")])],"isStart":false})});}
            var Q9;
            {var subQ0=sQuery(id+"F6.wireOp",EDGE,"E72.bottom");var subQ1=sQuery(id+"F6.wireOp",EDGE,"E72.top");Q9=makeQuery(id+"F7.boolean.opBoolean","COPY",FACE,{"disambiguationData":[TD([makeQuery(id+"F3.boolean.opBoolean","COPY",FACE,{"derivedFrom":makeQuery(id+"F3.opExtrude","SWEPT_FACE",FACE,{"disambiguationData":[OSD([sQuery(id+"F2.wireOp",EDGE,"E22.MirrorCS")])]})})])],"derivedFrom":makeQuery(id+"F7.opExtrude","CAP_FACE",FACE,{"disambiguationData":[OSD([subQ0,subQ1,sQuery(id+"F6.wireOp",EDGE,"E72.left"),sQuery(id+"F6.wireOp",EDGE,"E72.right")])],"isStart":false})});}
            var Q10;
            {var subQ0=sQuery(id+"F6.wireOp",EDGE,"E72.top");var subQ1=sQuery(id+"F6.wireOp",EDGE,"E72.bottom");Q10=makeQuery(id+"F7.boolean.opBoolean","COPY",FACE,{"disambiguationData":[TD([makeQuery(id+"F3.boolean.opBoolean","COPY",FACE,{"derivedFrom":makeQuery(id+"F3.opExtrude","SWEPT_FACE",FACE,{"disambiguationData":[OSD([sQuery(id+"F2.wireOp",EDGE,"E20.MirrorCS")])]})})])],"derivedFrom":makeQuery(id+"F7.opExtrude","CAP_FACE",FACE,{"disambiguationData":[OSD([subQ1,subQ0,sQuery(id+"F6.wireOp",EDGE,"E72.left"),sQuery(id+"F6.wireOp",EDGE,"E72.right")])],"isStart":false})});}
            var Q11;
            {var subQ0=sQuery(id+"F6.wireOp",EDGE,"E72.top");var subQ1=sQuery(id+"F6.wireOp",EDGE,"E72.bottom");Q11=makeQuery(id+"F7.boolean.opBoolean","COPY",FACE,{"disambiguationData":[TD([makeQuery(id+"F3.boolean.opBoolean","COPY",FACE,{"derivedFrom":makeQuery(id+"F3.opExtrude","SWEPT_FACE",FACE,{"disambiguationData":[OSD([sQuery(id+"F2.wireOp",EDGE,"E16.MirrorCS")])]})})])],"derivedFrom":makeQuery(id+"F7.opExtrude","CAP_FACE",FACE,{"disambiguationData":[OSD([subQ1,subQ0,sQuery(id+"F6.wireOp",EDGE,"E72.left"),sQuery(id+"F6.wireOp",EDGE,"E72.right")])],"isStart":false})});}
            var Q12;
            {var subQ0=sQuery(id+"F6.wireOp",EDGE,"E72.bottom");var subQ1=sQuery(id+"F6.wireOp",EDGE,"E72.top");Q12=makeQuery(id+"F7.boolean.opBoolean","COPY",FACE,{"disambiguationData":[TD([makeQuery(id+"F3.boolean.opBoolean","COPY",FACE,{"derivedFrom":makeQuery(id+"F3.opExtrude","SWEPT_FACE",FACE,{"disambiguationData":[OSD([sQuery(id+"F2.wireOp",EDGE,"E15.left")])]})})])],"derivedFrom":makeQuery(id+"F7.opExtrude","CAP_FACE",FACE,{"disambiguationData":[OSD([subQ0,subQ1,sQuery(id+"F6.wireOp",EDGE,"E72.left"),sQuery(id+"F6.wireOp",EDGE,"E72.right")])],"isStart":false})});}
            var Q13;
            {var subQ0=sQuery(id+"F6.wireOp",EDGE,"E72.bottom");var subQ1=sQuery(id+"F6.wireOp",EDGE,"E72.top");Q13=makeQuery(id+"F7.boolean.opBoolean","COPY",FACE,{"disambiguationData":[TD([makeQuery(id+"F3.boolean.opBoolean","COPY",FACE,{"derivedFrom":makeQuery(id+"F3.opExtrude","SWEPT_FACE",FACE,{"disambiguationData":[OSD([sQuery(id+"F2.wireOp",EDGE,"E18.MirrorCS")])]})})])],"derivedFrom":makeQuery(id+"F7.opExtrude","CAP_FACE",FACE,{"disambiguationData":[OSD([subQ0,subQ1,sQuery(id+"F6.wireOp",EDGE,"E72.left"),sQuery(id+"F6.wireOp",EDGE,"E72.right")])],"isStart":false})});}
            extrude(context, id + "F19", {"entities" : qUnion([Q0, Q1, Q2, Q3, Q4, Q5, Q6, Q7, Q8, Q9, Q10, Q11, Q12, Q13]), "operationType" : NewBodyOperationType.ADD, "depth" : 3.43 * mm, "offsetDistance" : 25.4 * mm});
        }
        {
            var Q0;
            Q0=makeQuery(id+"F1.opExtrude","CAP_FACE",FACE,{"disambiguationData":[OSD([sQuery(id+"F0.wireOp",EDGE,"E1.bottom"),sQuery(id+"F0.wireOp",EDGE,"E1.top"),sQuery(id+"F0.wireOp",EDGE,"E1.right"),sQuery(id+"F0.wireOp",EDGE,"E2.bottom"),sQuery(id+"F0.wireOp",EDGE,"E2.top"),sQuery(id+"F0.wireOp",EDGE,"E2.right")])],"isStart":true});
            var sketch = newSketch(context, id + "F20", { "sketchPlane" : qUnion([Q0])});
            skLineSegment(sketch, "E93.bottom", {"start": v(60.06, 47.87) * mm, "end": v(-59.81, 47.87) * mm});
            skLineSegment(sketch, "E93.top", {"start": v(60.06, 2.42) * mm, "end": v(-59.81, 2.42) * mm});
            skLineSegment(sketch, "E93.left", {"start": v(60.06, 47.87) * mm, "end": v(60.06, 2.42) * mm});
            skLineSegment(sketch, "E93.right", {"start": v(-59.81, 47.87) * mm, "end": v(-59.81, 2.42) * mm});
            skSolve(sketch);
        }
        {
            var Q0;
            Q0 = qSketchRegion(id + "F20", true);
            extrude(context, id + "F21", {"entities" : qUnion([Q0]), "operationType" : NewBodyOperationType.REMOVE, "depth" : 25.4 * mm, "offsetDistance" : 25.4 * mm});
        }
        {
            var Q0;
            Q0=makeQuery(id+"F1.opExtrude","SWEPT_FACE",FACE,{"disambiguationData":[OSD([sQuery(id+"F0.wireOp",EDGE,"E2.right")])]});
            var sketch = newSketch(context, id + "F22", { "sketchPlane" : qUnion([Q0])});
            skLineSegment(sketch, "E94", {"start": v(-4.4, 0) * mm, "end": v(-14.65, 0) * mm});
            skLineSegment(sketch, "E95", {"start": v(-14.65, 22.7) * mm, "end": v(-14.65, 17.78) * mm});
            skLineSegment(sketch, "E96", {"start": v(-4.4, 0) * mm, "end": v(-4.4, 7.62) * mm});
            skLineSegment(sketch, "E97", {"start": v(-4.4, 7.62) * mm, "end": v(-14.65, 7.62) * mm});
            skLineSegment(sketch, "E98", {"start": v(-4.4, 17.78) * mm, "end": v(-4.4, 25.4) * mm});
            skLineSegment(sketch, "E99", {"start": v(-4.4, 17.78) * mm, "end": v(-14.65, 17.78) * mm});
            skLineSegment(sketch, "E100", {"start": v(-14.65, 17.78) * mm, "end": v(-14.65, 25.4) * mm});
            skLineSegment(sketch, "E101", {"start": v(-4.4, 25.4) * mm, "end": v(-14.65, 25.4) * mm});
            skLineSegment(sketch, "E102.trimOffspring", {"start": v(-14.65, 7.62) * mm, "end": v(-14.65, 0) * mm});
            skSolve(sketch);
        }
        {
            var Q0;
            Q0 = qSketchRegion(id + "F22", true);
            extrude(context, id + "F23", {"entities" : qUnion([Q0]), "operationType" : NewBodyOperationType.ADD, "depth" : 12.7 * mm, "offsetDistance" : 25.4 * mm});
        }
        {
            var Q0;
            Q0=makeQuery(id+"F1.opExtrude","SWEPT_FACE",FACE,{"disambiguationData":[OSD([sQuery(id+"F0.wireOp",EDGE,"E1.right")])]});
            var sketch = newSketch(context, id + "F24", { "sketchPlane" : qUnion([Q0])});
            skLineSegment(sketch, "E103", {"start": v(2.54, 25.4) * mm, "end": v(14.65, 25.4) * mm});
            skLineSegment(sketch, "E104", {"start": v(14.65, 25.4) * mm, "end": v(14.65, 0) * mm});
            skLineSegment(sketch, "E105", {"start": v(14.65, 0) * mm, "end": v(2.54, 0) * mm});
            skLineSegment(sketch, "E106", {"start": v(2.54, 0) * mm, "end": v(2.54, 25.4) * mm});
            skSolve(sketch);
        }
        {
            var Q0;
            Q0 = qSketchRegion(id + "F24", true);
            extrude(context, id + "F25", {"entities" : qUnion([Q0]), "operationType" : NewBodyOperationType.ADD, "depth" : 12.7 * mm, "offsetDistance" : 25.4 * mm});
        }
        {
            var Q0;
            Q0=makeQuery(id+"F25.opExtrude","SWEPT_FACE",FACE,{"disambiguationData":[OSD([sQuery(id+"F24.wireOp",EDGE,"E103")])]});
            var sketch = newSketch(context, id + "F26", { "sketchPlane" : qUnion([Q0])});
            skLineSegment(sketch, "E107", {"start": v(-76.2, -2.54) * mm, "end": v(-63.5, -14.65) * mm});
            skCircle(sketch, "E108", {"center": v(-69.85, -8.6) * mm, "radius": 3.81 * mm});
            skSolve(sketch);
        }
        {
            var Q0;
            Q0 = qSketchRegion(id + "F26", true);
            extrude(context, id + "F27", {"entities" : qUnion([Q0]), "operationType" : NewBodyOperationType.REMOVE, "oppositeDirection" : true, "depth" : 25.4 * mm, "offsetDistance" : 25.4 * mm});
        }
        {
            var Q0;
            Q0=makeQuery(id+"F25.opExtrude","CAP_EDGE",EDGE,{"disambiguationData":[OSD([sQuery(id+"F24.wireOp",EDGE,"E106")])],"isStart":false});
            var Q1;
            Q1=makeQuery(id+"F25.opExtrude","CAP_EDGE",EDGE,{"disambiguationData":[OSD([sQuery(id+"F24.wireOp",EDGE,"E104")])],"isStart":false});
            var Q2;
            Q2=makeQuery(id+"F23.opExtrude","CAP_EDGE",EDGE,{"disambiguationData":[OSD([sQuery(id+"F22.wireOp",EDGE,"E100")])],"isStart":false});
            var Q3;
            Q3=makeQuery(id+"F23.opExtrude","CAP_EDGE",EDGE,{"disambiguationData":[OSD([sQuery(id+"F22.wireOp",EDGE,"E98")])],"isStart":false});
            var Q4;
            Q4=makeQuery(id+"F23.opExtrude","CAP_EDGE",EDGE,{"disambiguationData":[OSD([sQuery(id+"F22.wireOp",EDGE,"E96")])],"isStart":false});
            var Q5;
            Q5=makeQuery(id+"F23.opExtrude","CAP_EDGE",EDGE,{"disambiguationData":[OSD([sQuery(id+"F22.wireOp",EDGE,"E102.trimOffspring")])],"isStart":false});
            fillet(context, id + "F28", {"entities" : qUnion([Q0, Q1, Q2, Q3, Q4, Q5]), "radius" : 6.35 * mm, "tangentPropagation" : true, "allowEdgeOverflow" : false});
        }
        {
            var Q0;
            Q0=makeQuery(id+"F25.opExtrude","SWEPT_FACE",FACE,{"disambiguationData":[OSD([sQuery(id+"F24.wireOp",EDGE,"E104")])]});
            var sketch = newSketch(context, id + "F29", { "sketchPlane" : qUnion([Q0])});
            skLineSegment(sketch, "E109", {"start": v(-63.5, 12.7) * mm, "end": v(-83.31, 12.7) * mm});
            skLineSegment(sketch, "E110", {"start": v(-83.31, 12.7) * mm, "end": v(-83.31, 17.78) * mm});
            skLineSegment(sketch, "E111", {"start": v(-83.31, 12.7) * mm, "end": v(-83.31, 7.62) * mm});
            skLineSegment(sketch, "E112", {"start": v(-83.31, 17.78) * mm, "end": v(-63.5, 17.78) * mm});
            skLineSegment(sketch, "E113", {"start": v(-83.31, 7.62) * mm, "end": v(-63.5, 7.62) * mm});
            skLineSegment(sketch, "E114", {"start": v(-63.5, 7.62) * mm, "end": v(-63.5, 17.78) * mm});
            skSolve(sketch);
        }
        {
            var Q0;
            Q0 = qSketchRegion(id + "F29", true);
            extrude(context, id + "F30", {"entities" : qUnion([Q0]), "operationType" : NewBodyOperationType.REMOVE, "oppositeDirection" : true, "depth" : 25.4 * mm, "offsetDistance" : 25.4 * mm});
        }
        {
            var Q0;
            Q0=makeQuery(id+"F23.opExtrude","SWEPT_FACE",FACE,{"disambiguationData":[OSD([sQuery(id+"F22.wireOp",EDGE,"E101")])]});
            var sketch = newSketch(context, id + "F31", { "sketchPlane" : qUnion([Q0])});
            skLineSegment(sketch, "E115", {"start": v(76.08, -9.53) * mm, "end": v(73.03, -9.53) * mm});
            skCircle(sketch, "E116", {"center": v(69.22, -9.55) * mm, "radius": 3.81 * mm});
            skSolve(sketch);
        }
        {
            var Q0;
            Q0=makeQuery(id+"F31.imprint","IMPRINT",FACE,{"disambiguationData":[TD([[makeQuery(id+"F31.imprint","IMPRINT",EDGE,{"derivedFrom":sQuery(id+"F31.wireOp",EDGE,"E116")}),1.0]])]});
            extrude(context, id + "F32", {"entities" : qUnion([Q0]), "operationType" : NewBodyOperationType.REMOVE, "oppositeDirection" : true, "depth" : 25.4 * mm, "offsetDistance" : 25.4 * mm});
        }
        {
            var Q0;
            Q0=makeQuery(id+"F28.opFillet","BLEND_EDGE",EDGE,{"blendedFrom":[makeQuery(id+"F23.opExtrude","CAP_EDGE",EDGE,{"disambiguationData":[OSD([sQuery(id+"F22.wireOp",EDGE,"E98")])],"isStart":false}),makeQuery(id+"F23.opExtrude","CAP_EDGE",EDGE,{"disambiguationData":[OSD([sQuery(id+"F22.wireOp",EDGE,"E100")])],"isStart":false})],"blendedInto":[]});
            var Q1;
            Q1=makeQuery(id+"F28.opFillet","BLEND_EDGE",EDGE,{"blendedFrom":[makeQuery(id+"F23.opExtrude","CAP_EDGE",EDGE,{"disambiguationData":[OSD([sQuery(id+"F22.wireOp",EDGE,"E96")])],"isStart":false}),makeQuery(id+"F23.opExtrude","CAP_EDGE",EDGE,{"disambiguationData":[OSD([sQuery(id+"F22.wireOp",EDGE,"E102.trimOffspring")])],"isStart":false})],"blendedInto":[]});
            fillet(context, id + "F33", {"entities" : qUnion([Q0, Q1]), "radius" : 5.08 * mm, "tangentPropagation" : true, "allowEdgeOverflow" : false});
        }
    });
